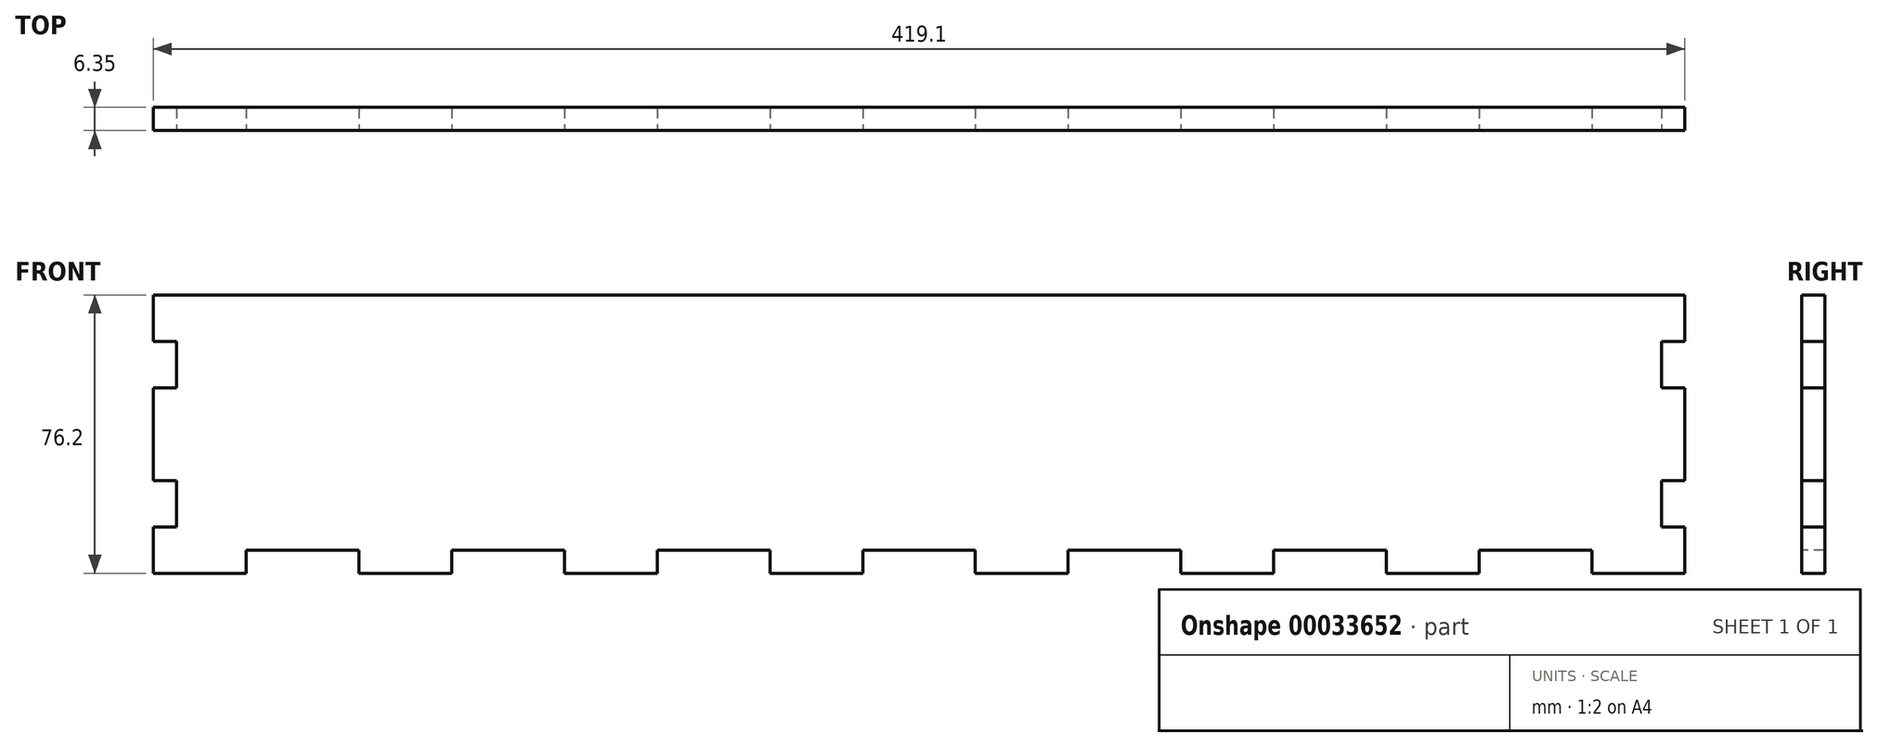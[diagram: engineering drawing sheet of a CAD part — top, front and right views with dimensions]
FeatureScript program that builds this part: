
annotation { "Feature Type Name" : "Feature", "Feature Type Description" : "" }
export const myFeature = defineFeature(function(context is Context, id is Id, definition is map)
    precondition{}
    {
        {
            var Q0;
            Q0=qCreatedBy(makeId("Front.planeOp"),FACE);
            var sketch = newSketch(context, id + "F0", { "sketchPlane" : qUnion([Q0])});
            skLineSegment(sketch, "E0.rect.bottom", {"start": v(-209.55, 38.1) * mm, "end": v(209.55, 38.1) * mm});
            skLineSegment(sketch, "E0.rect.top", {"start": v(-209.55, -38.1) * mm, "end": v(209.55, -38.1) * mm});
            skLineSegment(sketch, "E0.rect.left", {"start": v(-209.55, 38.1) * mm, "end": v(-209.55, -38.1) * mm});
            skLineSegment(sketch, "E0.rect.right", {"start": v(209.55, 38.1) * mm, "end": v(209.55, -38.1) * mm});
            skPoint(sketch, "E0.rect.middle", {"position": v(0, 0) * mm});
            skSolve(sketch);
        }
        {
            var Q0;
            Q0=qSketchRegion(id+"F0",true);
            extrude(context, id + "F1", {"entities" : qUnion([Q0]), "depth" : 6.35 * mm});
        }
        {
            var Q0;
            Q0=makeQuery(id+"F1.opExtrude","CAP_FACE",FACE,{"disambiguationData":[OSD([sQuery(id+"F0.wireOp",EDGE,"E0.rect.bottom"),sQuery(id+"F0.wireOp",EDGE,"E0.rect.top"),sQuery(id+"F0.wireOp",EDGE,"E0.rect.left"),sQuery(id+"F0.wireOp",EDGE,"E0.rect.right")])],"isStart":false});
            var sketch = newSketch(context, id + "F2", { "sketchPlane" : qUnion([Q0])});
            skLineSegment(sketch, "E1.bottom", {"start": v(-184.15, -38.1) * mm, "end": v(-153.3, -38.1) * mm});
            skLineSegment(sketch, "E1.top", {"start": v(-184.15, -31.75) * mm, "end": v(-153.3, -31.75) * mm});
            skLineSegment(sketch, "E1.left", {"start": v(-184.15, -38.1) * mm, "end": v(-184.15, -31.75) * mm});
            skLineSegment(sketch, "E1.right", {"start": v(-153.3, -38.1) * mm, "end": v(-153.3, -31.75) * mm});
            skLineSegment(sketch, "E2.1.0.0", {"start": v(-127.9, -38.1) * mm, "end": v(-97.06, -38.1) * mm});
            skLineSegment(sketch, "E2.1.0.1", {"start": v(-127.9, -31.75) * mm, "end": v(-97.06, -31.75) * mm});
            skLineSegment(sketch, "E2.1.0.2", {"start": v(-127.9, -38.1) * mm, "end": v(-127.9, -31.75) * mm});
            skLineSegment(sketch, "E2.1.0.3", {"start": v(-97.06, -38.1) * mm, "end": v(-97.06, -31.75) * mm});
            skLineSegment(sketch, "E2.2.0.0", {"start": v(-71.66, -38.1) * mm, "end": v(-40.82, -38.1) * mm});
            skLineSegment(sketch, "E2.2.0.1", {"start": v(-71.66, -31.75) * mm, "end": v(-40.82, -31.75) * mm});
            skLineSegment(sketch, "E2.2.0.2", {"start": v(-71.66, -38.1) * mm, "end": v(-71.66, -31.75) * mm});
            skLineSegment(sketch, "E2.2.0.3", {"start": v(-40.82, -38.1) * mm, "end": v(-40.82, -31.75) * mm});
            skLineSegment(sketch, "E2.3.0.0", {"start": v(-15.42, -38.1) * mm, "end": v(15.42, -38.1) * mm});
            skLineSegment(sketch, "E2.3.0.1", {"start": v(-15.42, -31.75) * mm, "end": v(15.42, -31.75) * mm});
            skLineSegment(sketch, "E2.3.0.2", {"start": v(-15.42, -38.1) * mm, "end": v(-15.42, -31.75) * mm});
            skLineSegment(sketch, "E2.3.0.3", {"start": v(15.42, -38.1) * mm, "end": v(15.42, -31.75) * mm});
            skLineSegment(sketch, "E2.4.0.0", {"start": v(40.82, -38.1) * mm, "end": v(71.66, -38.1) * mm});
            skLineSegment(sketch, "E2.4.0.1", {"start": v(40.82, -31.75) * mm, "end": v(71.66, -31.75) * mm});
            skLineSegment(sketch, "E2.4.0.2", {"start": v(40.82, -38.1) * mm, "end": v(40.82, -31.75) * mm});
            skLineSegment(sketch, "E2.4.0.3", {"start": v(71.66, -38.1) * mm, "end": v(71.66, -31.75) * mm});
            skLineSegment(sketch, "E2.5.0.0", {"start": v(97.06, -38.1) * mm, "end": v(127.9, -38.1) * mm});
            skLineSegment(sketch, "E2.5.0.1", {"start": v(97.06, -31.75) * mm, "end": v(127.9, -31.75) * mm});
            skLineSegment(sketch, "E2.5.0.2", {"start": v(97.06, -38.1) * mm, "end": v(97.06, -31.75) * mm});
            skLineSegment(sketch, "E2.5.0.3", {"start": v(127.9, -38.1) * mm, "end": v(127.9, -31.75) * mm});
            skLineSegment(sketch, "E2.6.0.0", {"start": v(153.3, -38.1) * mm, "end": v(184.15, -38.1) * mm});
            skLineSegment(sketch, "E2.6.0.1", {"start": v(153.3, -31.75) * mm, "end": v(184.15, -31.75) * mm});
            skLineSegment(sketch, "E2.6.0.2", {"start": v(153.3, -38.1) * mm, "end": v(153.3, -31.75) * mm});
            skLineSegment(sketch, "E2.6.0.3", {"start": v(184.15, -38.1) * mm, "end": v(184.15, -31.75) * mm});
            skLineSegment(sketch, "E2.direction1", {"start": v(-184.15, -38.1) * mm, "end": v(-127.9, -38.1) * mm, "construction": true});
            skLineSegment(sketch, "E3.bottom", {"start": v(-209.55, -25.4) * mm, "end": v(-203.2, -25.4) * mm});
            skLineSegment(sketch, "E3.top", {"start": v(-209.55, -12.7) * mm, "end": v(-203.2, -12.7) * mm});
            skLineSegment(sketch, "E3.left", {"start": v(-209.55, -25.4) * mm, "end": v(-209.55, -12.7) * mm});
            skLineSegment(sketch, "E3.right", {"start": v(-203.2, -25.4) * mm, "end": v(-203.2, -12.7) * mm});
            skLineSegment(sketch, "E4.bottom", {"start": v(-209.55, 25.4) * mm, "end": v(-203.2, 25.4) * mm});
            skLineSegment(sketch, "E4.top", {"start": v(-209.55, 12.7) * mm, "end": v(-203.2, 12.7) * mm});
            skLineSegment(sketch, "E4.left", {"start": v(-209.55, 25.4) * mm, "end": v(-209.55, 12.7) * mm});
            skLineSegment(sketch, "E4.right", {"start": v(-203.2, 25.4) * mm, "end": v(-203.2, 12.7) * mm});
            skLineSegment(sketch, "E5", {"start": v(0, 38.1) * mm, "end": v(0, -38.1) * mm, "construction": true});
            skLineSegment(sketch, "E6.MirrorCS", {"start": v(203.2, 25.4) * mm, "end": v(203.2, 12.7) * mm});
            skLineSegment(sketch, "E7.MirrorCS", {"start": v(209.55, -25.4) * mm, "end": v(203.2, -25.4) * mm});
            skLineSegment(sketch, "E8.MirrorCS", {"start": v(209.55, 25.4) * mm, "end": v(209.55, 12.7) * mm});
            skLineSegment(sketch, "E9.MirrorCS", {"start": v(203.2, -25.4) * mm, "end": v(203.2, -12.7) * mm});
            skLineSegment(sketch, "E10.MirrorCS", {"start": v(209.55, -12.7) * mm, "end": v(203.2, -12.7) * mm});
            skLineSegment(sketch, "E11.MirrorCS", {"start": v(209.55, 25.4) * mm, "end": v(203.2, 25.4) * mm});
            skLineSegment(sketch, "E12.MirrorCS", {"start": v(209.55, 12.7) * mm, "end": v(203.2, 12.7) * mm});
            skLineSegment(sketch, "E13.MirrorCS", {"start": v(209.55, -25.4) * mm, "end": v(209.55, -12.7) * mm});
            skSolve(sketch);
        }
        {
            var Q0;
            Q0=qSketchRegion(id+"F2",true);
            extrude(context, id + "F3", {"entities" : qUnion([Q0]), "operationType" : NewBodyOperationType.REMOVE, "endBound" : BoundingType.THROUGH_ALL, "oppositeDirection" : true, "depth" : 25.4 * mm});
        }
    });
